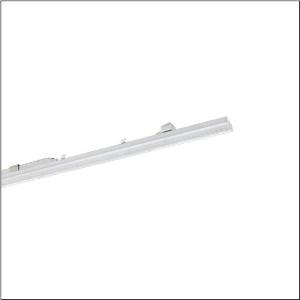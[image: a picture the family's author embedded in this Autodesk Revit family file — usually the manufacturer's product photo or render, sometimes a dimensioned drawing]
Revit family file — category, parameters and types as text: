
# Revit family: tl_l_5wd7a8f0h2c5
name_source: partatom
category: Lighting Fixtures
units: mm (PartAtom-declared; Revit-internal decimal feet)

## family parameters
Cut with Voids When Loaded = No
Host = Face
Light Source = No
Part Type = Normal
Room Calculation Point = No
Round Connector Dimension = Use Diameter
Shared = No

## types (1)
- TL L (1 x LED, 9800 lm, 63.3 W, 4000K)
    Apparent Load = 63 VA
    CIE Flux Codes = 49 84 98 100 100
    Color Rendering = 80
    Color Temperature = 4000K
    Default Elevation = 1800 mm
    Description = TL L, luminaire insert, of sheet steel, galvanised, coil coated, white, length: 1.500mm, width: 66mm, height: 67mm, surge protection,LED rated luminous flux: 9.800lm, light colour: 840, control gear: 4..20mA, with terminal, 5-pole, mains connection: 230..240V, AC, 50/60Hz, rated input power: 63W, micro fuse,primary optical cover: cover, of PMMA, light emission: direct distribution, protection rating (complete): as luminaire, insulation class (complete): insulation class I (protective earthing), certification: CE, impact resistance: IK06, permissible ambient temperature for indoor applications: -25..+35°C, packaging unit: 1 piece
    Height = 120 mm
    Lamp = 1 x LED
    Lamp Light Flux = 9800 lm
    Lamp Power = 63.3 W
    Lamp count = 1
    Length = 1690 mm
    Luminous efficacy = 155 lm/W
    Manufacturer = Siteco
    ModVariant = No
    Model = 5WD7A8F0H2C5
    Mounting Place = Ceiling
    Mounting Type = Pendant
    Number of Poles = 1
    OnlyDefault = Yes
    Power Factor = 1
    Product Name = TL L
    Product group = luminaire insert
    ProductGroupID = 901
    Protection Class = Protection class I
    Protection Degree = Degree of protection
    RLX_Detail_Level = 1
    RLX_Emergency_Light_Flux = 0 lm
    RLX_Emergency_Type = 0
    RLX_Emergency_Type_DB = No
    RlxData = <blob elided: 14153 chars, md5=4dbbea92>
    Socket = socket
    Standby Power = 0 W
    System Light Flux = 9800 lm
    System Power = 63 W
    Type Comments = Product without accessories
    Type Image = l_1294382.jpg
    URL = http://relux.com
    VarID = ---
    Voltage = 0 V
    Weight = 0.00 kg
    Width = 208 mm

## geometry (parser evidence)
native form markers: Sweep x12
no freeform markers — native parametric forms only
